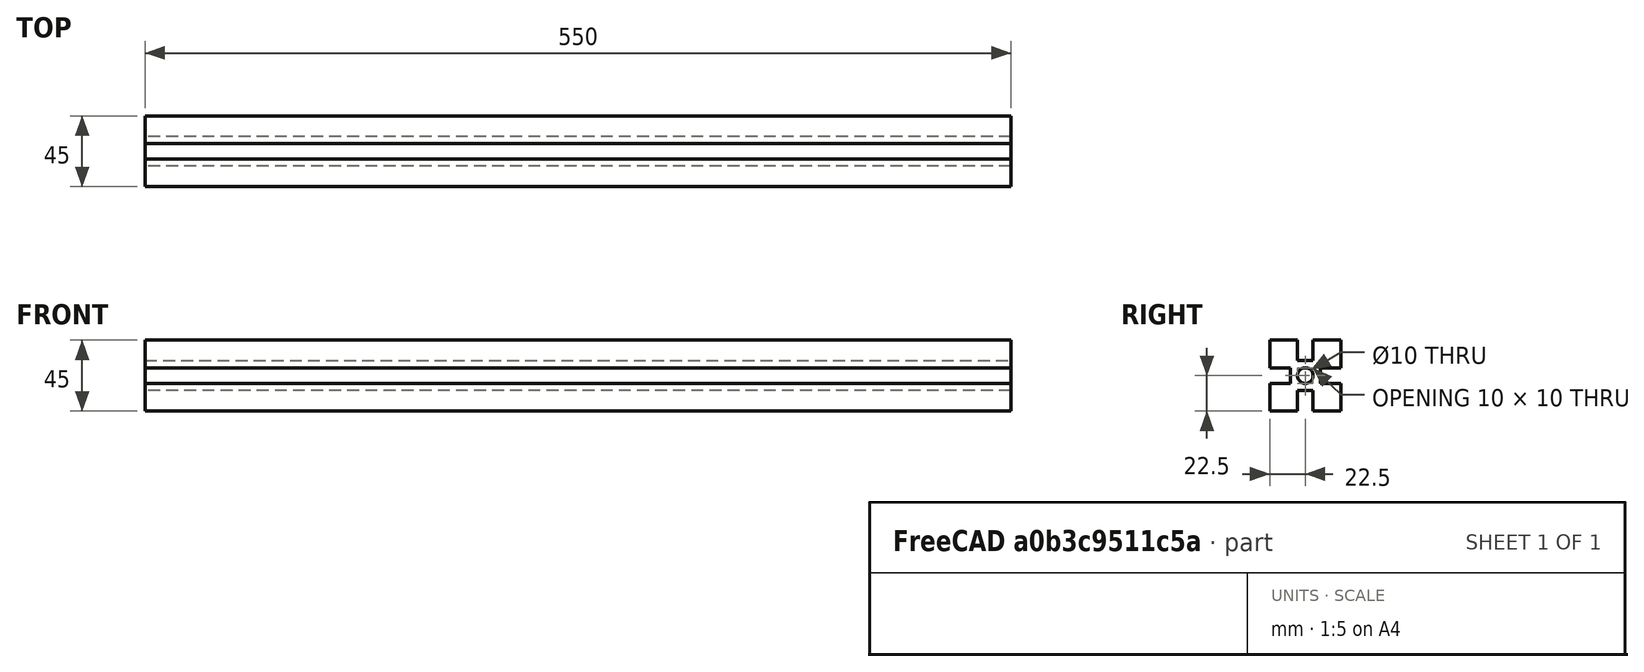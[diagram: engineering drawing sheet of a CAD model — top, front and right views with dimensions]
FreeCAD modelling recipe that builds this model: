
FCSTD DOCUMENT  (FreeCAD 1.0R39109 (Git))
Label: vslot 45x45x585
License: All rights reserved
LicenseURL: https://en.wikipedia.org/wiki/All_rights_reserved
objects: PartDesign::Pocket×2, Part::Feature×1, PartDesign::FeatureBase×1, PartDesign::Pad×1, PartDesign::Body×1
note: 13 computed .brp shape members not serialized (recipe doc carries the construction recipe); baked Part::Feature solids carry a one-line shape summary decoded from their .brp

FEATURE [Part::Feature] Part__Feature  label="1"
  shape: bbox 1000 x 45 x 45 mm, 24 faces (baked)
FEATURE [PartDesign::FeatureBase] BaseFeature
  BaseFeature = -> Part__Feature
  Suppressed = false
FEATURE [PartDesign::Pocket] Pocket
  BaseFeature = -> BaseFeature
  Direction = (1,0,0)
  Length = 460
  Length2 = 5
  Profile = -> BaseFeature [Face23]
  Refine = true
  Suppressed = false
  Type = 0
FEATURE [PartDesign::Pad] Pad
  BaseFeature = -> Pocket
  Direction = (-1,0,0)
  Length = 45
  Length2 = 10
  Profile = -> Pocket [Face1]
  Refine = true
  Suppressed = false
  Type = 0
FEATURE [PartDesign::Pocket] Pocket001
  BaseFeature = -> Pad
  Direction = (1,0,0)
  Length = 35
  Length2 = 5
  Profile = -> Pad [Face3]
  Refine = true
  Suppressed = false
  Type = 0
FEATURE [PartDesign::Body] Body
  AllowCompound = false
  BaseFeature = -> Part__Feature
  Group = -> [BaseFeature,Pocket,Pad,Pocket001]
  Origin = -> Origin
  Tip = -> Pocket001
